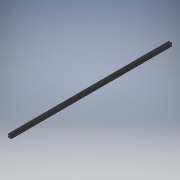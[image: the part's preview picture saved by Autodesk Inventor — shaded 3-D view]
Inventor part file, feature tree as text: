
AUTODESK INVENTOR PART (.ipt)
format: ipt  version: 2019 (Build 230136000, 136)  size: 191,488 bytes
history: native  units: mm
features: other x7, extrude x1, sketch x1
ambient origin geometry x8: Origin, YZ Plane, XZ Plane, XY Plane, X Axis, Y Axis, Z Axis, Center Point
bodies: Solid1 (feature_tree)
feature tree (9):
  extrude  "Extrusion1"  TaperAngle=0.0deg  [1 undecoded]
  other  "to_frame_XY"
  other  "to_frame_YZ"
  other  "to_frame_ZX"
  other  "to_frame_X"
  other  "to_frame_Y"
  other  "to_frame_Z"
  other  "to_frame_Center"
  sketch  "Sketch_5"  dims[d0=1000.0mm d1=0.0mm d2=0.0mm]
note: 1 required parameter value undecoded (feature->parameter linkage not recoverable at this tier; creation-order binding heuristic only, values carry confidence <= 0.55)
